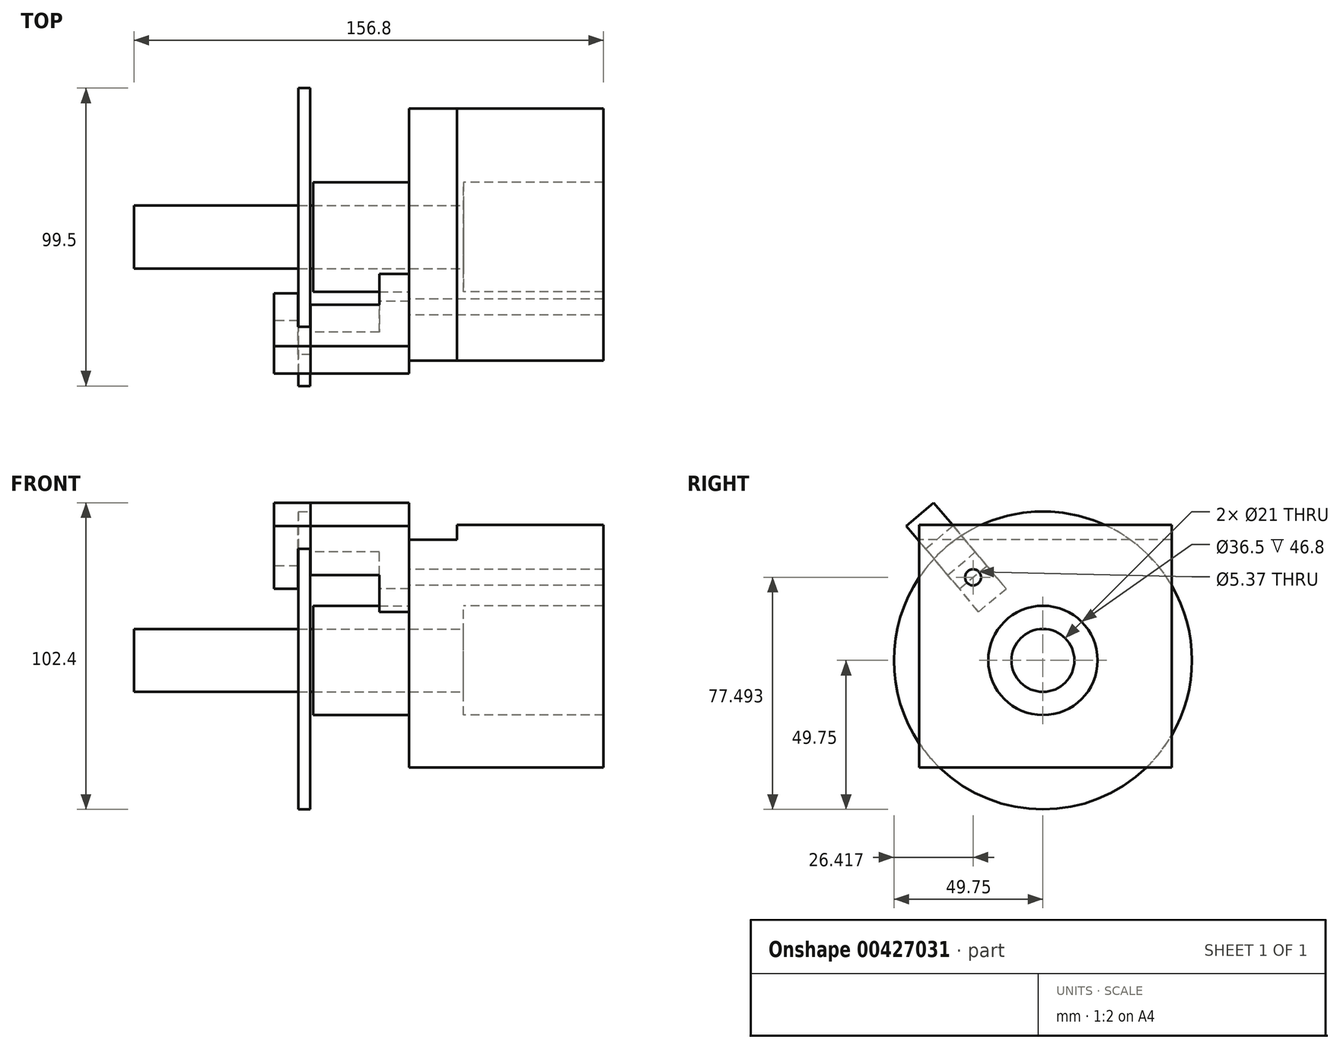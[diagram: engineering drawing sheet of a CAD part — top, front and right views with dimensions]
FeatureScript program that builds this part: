
annotation { "Feature Type Name" : "Feature", "Feature Type Description" : "" }
export const myFeature = defineFeature(function(context is Context, id is Id, definition is map)
    precondition{}
    {
        {
            var Q0;
            Q0=qCreatedBy(makeId("Right.planeOp"),FACE);
            var sketch = newSketch(context, id + "F0", { "sketchPlane" : qUnion([Q0])});
            skCircle(sketch, "E0", {"center": v(0, 0) * mm, "radius": 18.25 * mm});
            skCircle(sketch, "E1", {"center": v(0, 0) * mm, "radius": 10.5 * mm});
            skLineSegment(sketch, "E2.bottom", {"start": v(42.96, 45.25) * mm, "end": v(-41.28, 45.25) * mm});
            skLineSegment(sketch, "E2.top", {"start": v(42.96, -35.7) * mm, "end": v(-41.28, -35.7) * mm});
            skLineSegment(sketch, "E2.left", {"start": v(42.96, 45.25) * mm, "end": v(42.96, -35.7) * mm});
            skLineSegment(sketch, "E2.right", {"start": v(-41.28, 45.25) * mm, "end": v(-41.28, -35.7) * mm});
            skLineSegment(sketch, "E3.top", {"start": v(42.96, 40.25) * mm, "end": v(-41.28, 40.25) * mm});
            skLineSegment(sketch, "E3.left", {"start": v(42.96, 45.25) * mm, "end": v(42.96, 40.25) * mm});
            skLineSegment(sketch, "E3.right", {"start": v(-41.28, 45.25) * mm, "end": v(-41.28, 40.25) * mm});
            skCircle(sketch, "E4", {"center": v(-23.33, 27.74) * mm, "radius": 2.68 * mm});
            skSolve(sketch);
        }
        {
            var Q0;
            Q0=makeQuery(id+"F0.imprint","IMPRINT",FACE,{"disambiguationData":[TD([[makeQuery(id+"F0.imprint","IMPRINT",EDGE,{"derivedFrom":sQuery(id+"F0.wireOp",EDGE,"E0")}),-1.0]])]});
            extrude(context, id + "F1", {"entities" : qUnion([Q0]), "depth" : 64.9 * mm});
        }
        {
            var Q0;
            Q0=makeQuery(id+"F0.imprint","IMPRINT",FACE,{"disambiguationData":[TD([[makeQuery(id+"F0.imprint","IMPRINT",EDGE,{"derivedFrom":sQuery(id+"F0.wireOp",EDGE,"E2.bottom")}),1.0]])]});
            var Q1;
            Q1=makeQuery(id+"F1.opExtrude","CAP_FACE",FACE,{"disambiguationData":[OSD([sQuery(id+"F0.wireOp",EDGE,"E0"),sQuery(id+"F0.wireOp",EDGE,"E2.top"),sQuery(id+"F0.wireOp",EDGE,"E2.left"),sQuery(id+"F0.wireOp",EDGE,"E2.right"),sQuery(id+"F0.wireOp",EDGE,"E3.top"),sQuery(id+"F0.wireOp",EDGE,"E4")])],"isStart":false});
            extrude(context, id + "F2", {"entities" : qUnion([Q0]), "operationType" : NewBodyOperationType.ADD, "endBound" : BoundingType.UP_TO_SURFACE, "endBoundEntityFace" : qUnion([Q1]), "depth" : 69.1 * mm, "hasSecondDirection" : true, "secondDirectionOppositeDirection" : false, "secondDirectionDepth" : 16 * mm});
        }
        {
            var Q0;
            Q0=makeQuery(id+"F0.imprint","IMPRINT",FACE,{"disambiguationData":[TD([[makeQuery(id+"F0.imprint","IMPRINT",EDGE,{"derivedFrom":sQuery(id+"F0.wireOp",EDGE,"E0")}),1.0]])]});
            extrude(context, id + "F3", {"entities" : qUnion([Q0]), "operationType" : NewBodyOperationType.ADD, "oppositeDirection" : true, "depth" : 32 * mm, "hasSecondDirection" : true, "secondDirectionOppositeDirection" : false, "secondDirectionDepth" : 18.1 * mm});
        }
        {
            var Q0;
            Q0=makeQuery(id+"F0.imprint","IMPRINT",FACE,{"disambiguationData":[TD([[makeQuery(id+"F0.imprint","IMPRINT",EDGE,{"derivedFrom":sQuery(id+"F0.wireOp",EDGE,"E1")}),1.0]])]});
            extrude(context, id + "F4", {"entities" : qUnion([Q0]), "oppositeDirection" : true, "depth" : 91.9 * mm});
        }
        {
            var Q0;
            Q0=makeQuery(id+"F3.opExtrude","CAP_FACE",FACE,{"disambiguationData":[OSD([sQuery(id+"F0.wireOp",EDGE,"E0"),sQuery(id+"F0.wireOp",EDGE,"E1")])],"isStart":false});
            cPlane(context, id + "F5", {"entities" : qUnion([Q0]), "cplaneType" : CPlaneType.OFFSET, "offset" : 1 * mm, "width" : 150 * mm, "height" : 150 * mm});
        }
        {
            var Q0;
            Q0=qCreatedBy(id+"F5.planeOp",FACE);
            var sketch = newSketch(context, id + "F6", { "sketchPlane" : qUnion([Q0])});
            skCircle(sketch, "E5", {"center": v(0, 0) * mm, "radius": 49.75 * mm});
            skCircle(sketch, "E6.0", {"center": v(0, 0) * mm, "radius": 10.5 * mm});
            skSolve(sketch);
        }
        {
            var Q0;
            Q0=makeQuery(id+"F6.imprint","IMPRINT",FACE,{"disambiguationData":[TD([[makeQuery(id+"F6.imprint","IMPRINT",EDGE,{"derivedFrom":sQuery(id+"F6.wireOp",EDGE,"E5")}),1.0]])]});
            extrude(context, id + "F7", {"entities" : qUnion([Q0]), "depth" : 4 * mm});
        }
        {
            var Q0;
            Q0=sQuery(id+"F0.wireOp",VERTEX,"E4.center");
            var Q1;
            Q1=qCreatedBy(makeId("Origin.pointOp"),VERTEX);
            var Q2;
            Q2=sQuery(id+"F6.wireOp",VERTEX,"E5.center");
            cPlane(context, id + "F8", {"entities" : qUnion([Q0, Q1, Q2]), "cplaneType" : CPlaneType.THREE_POINT, "offset" : 25 * mm, "width" : 150 * mm, "height" : 150 * mm});
        }
        {
            var Q0;
            Q0=qCreatedBy(id+"F8.planeOp",FACE);
            var sketch = newSketch(context, id + "F9", { "sketchPlane" : qUnion([Q0])});
            skPoint(sketch, "E7.0", {"position": v(0, 36.25) * mm});
            skLineSegment(sketch, "E8", {"start": v(0, 26.25) * mm, "end": v(-10, 26.25) * mm});
            skLineSegment(sketch, "E9", {"start": v(-10, 26.25) * mm, "end": v(-10, 42.25) * mm});
            skLineSegment(sketch, "E10", {"start": v(-10, 42.25) * mm, "end": v(-32.9, 42.25) * mm});
            skLineSegment(sketch, "E11", {"start": v(-32.9, 42.25) * mm, "end": v(-32.9, 53.75) * mm});
            skLineSegment(sketch, "E12", {"start": v(-32.9, 53.75) * mm, "end": v(-37.1, 53.75) * mm});
            skLineSegment(sketch, "E13", {"start": v(-37.1, 53.75) * mm, "end": v(-37.1, 36.25) * mm});
            skLineSegment(sketch, "E14", {"start": v(-37.1, 36.25) * mm, "end": v(-45.1, 36.25) * mm});
            skLineSegment(sketch, "E15", {"start": v(-45.1, 36.25) * mm, "end": v(-45.1, 63.75) * mm});
            skLineSegment(sketch, "E16", {"start": v(-45.1, 63.75) * mm, "end": v(0, 63.75) * mm});
            skLineSegment(sketch, "E17", {"start": v(0, 63.75) * mm, "end": v(0, 26.25) * mm});
            skLineSegment(sketch, "E18", {"start": v(-37, 49.75) * mm, "end": v(-33, 49.75) * mm});
            skLineSegment(sketch, "E19", {"start": v(-37, 49.75) * mm, "end": v(-33, 49.75) * mm, "construction": true});
            skLineSegment(sketch, "E20", {"start": v(-32.9, 53.75) * mm, "end": v(-32.9, 63.75) * mm});
            skSolve(sketch);
        }
        {
            var Q0;
            Q0=makeQuery(id+"F9.imprint","IMPRINT",FACE,{"disambiguationData":[TD([[makeQuery(id+"F9.imprint","IMPRINT",EDGE,{"derivedFrom":sQuery(id+"F9.wireOp",EDGE,"E8")}),-1.0]])]});
            extrude(context, id + "F10", {"entities" : qUnion([Q0]), "depth" : 12 * mm, "symmetric" : true});
        }
        {
            var Q0;
            Q0=makeQuery(id+"F9.imprint","IMPRINT",FACE,{"disambiguationData":[TD([[makeQuery(id+"F9.imprint","IMPRINT",EDGE,{"derivedFrom":sQuery(id+"F9.wireOp",EDGE,"E12")}),-1.0]])]});
            extrude(context, id + "F11", {"entities" : qUnion([Q0]), "depth" : 12 * mm, "symmetric" : true});
        }
    });
